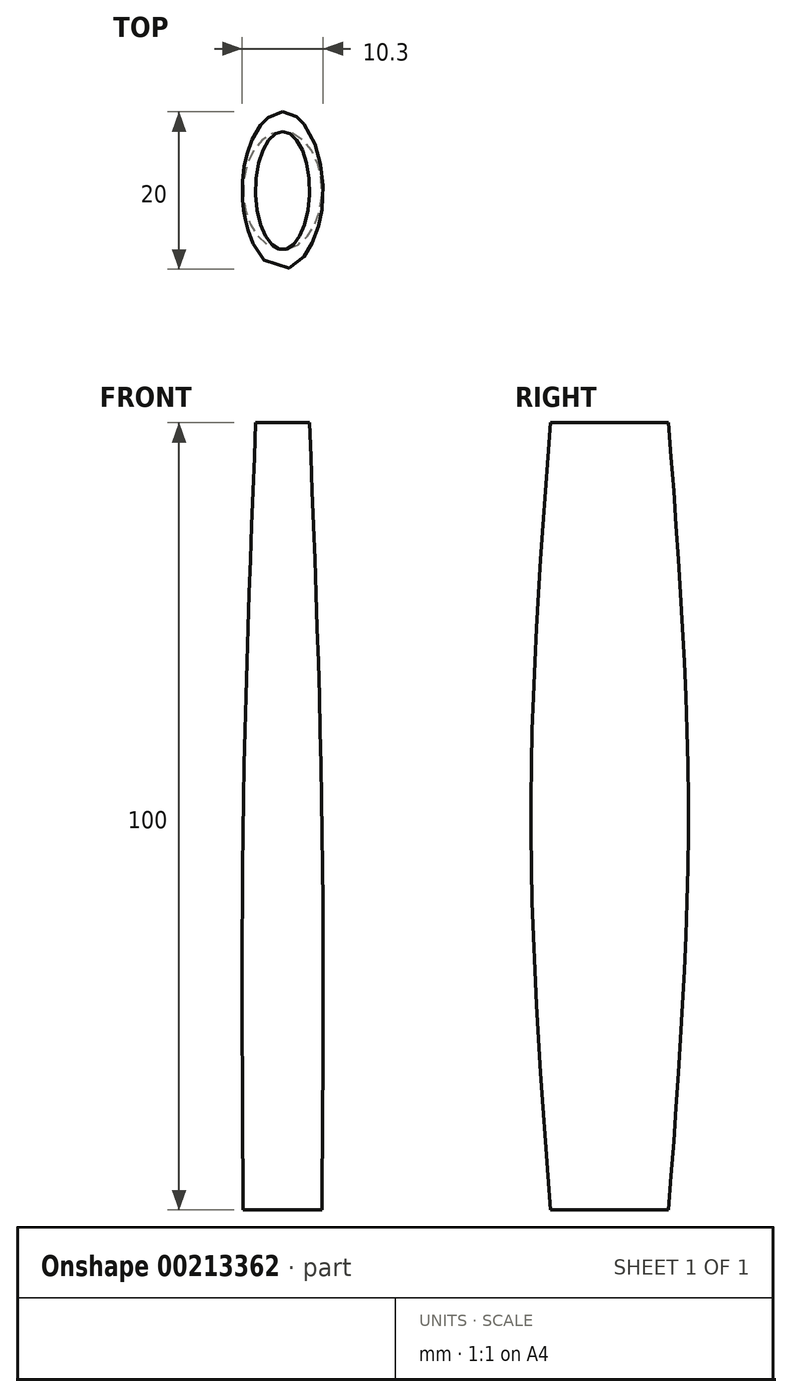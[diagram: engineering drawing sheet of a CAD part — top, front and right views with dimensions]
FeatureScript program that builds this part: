
annotation { "Feature Type Name" : "Feature", "Feature Type Description" : "" }
export const myFeature = defineFeature(function(context is Context, id is Id, definition is map)
    precondition{}
    {
        {
            var Q0;
            Q0=qCreatedBy(makeId("Top.planeOp"),FACE);
            cPlane(context, id + "F0", {"entities" : qUnion([Q0]), "cplaneType" : CPlaneType.OFFSET, "offset" : 50 * mm, "width" : 150 * mm, "height" : 150 * mm});
        }
        {
            var Q0;
            Q0=qCreatedBy(makeId("Top.planeOp"),FACE);
            cPlane(context, id + "F1", {"entities" : qUnion([Q0]), "cplaneType" : CPlaneType.OFFSET, "offset" : 50 * mm, "oppositeDirection" : true, "width" : 150 * mm, "height" : 150 * mm});
        }
        {
            var Q0;
            Q0=qCreatedBy(makeId("Top.planeOp"),FACE);
            var sketch = newSketch(context, id + "F2", { "sketchPlane" : qUnion([Q0])});
            skEllipse(sketch, "E0", {"center": v(0, 0) * mm, "majorRadius": 10 * mm, "minorRadius": 5 * mm, "majorAxis": v(0, 1)});
            skSolve(sketch);
        }
        {
            var Q0;
            Q0=qCreatedBy(id+"F0.planeOp",FACE);
            var sketch = newSketch(context, id + "F3", { "sketchPlane" : qUnion([Q0])});
            skEllipse(sketch, "E1", {"center": v(0, 0) * mm, "majorRadius": 7.5 * mm, "minorRadius": 3.42 * mm, "majorAxis": v(0, 1)});
            skSolve(sketch);
        }
        {
            var Q0;
            Q0=qCreatedBy(id+"F1.planeOp",FACE);
            var sketch = newSketch(context, id + "F4", { "sketchPlane" : qUnion([Q0])});
            skEllipse(sketch, "E2", {"center": v(0, 0) * mm, "majorRadius": 7.5 * mm, "minorRadius": 5 * mm, "majorAxis": v(0, -1)});
            skSolve(sketch);
        }
        {
            var Q0;
            Q0=makeQuery(id+"F3.imprint","IMPRINT",FACE,{"disambiguationData":[TD([[makeQuery(id+"F3.imprint","IMPRINT",EDGE,{"derivedFrom":sQuery(id+"F3.wireOp",EDGE,"E1")}),1.0]])]});
            var Q1;
            Q1=makeQuery(id+"F2.imprint","IMPRINT",FACE,{"disambiguationData":[TD([[makeQuery(id+"F2.imprint","IMPRINT",EDGE,{"derivedFrom":sQuery(id+"F2.wireOp",EDGE,"E0")}),1.0]])]});
            var Q2;
            Q2=makeQuery(id+"F4.imprint","IMPRINT",FACE,{"disambiguationData":[TD([[makeQuery(id+"F4.imprint","IMPRINT",EDGE,{"derivedFrom":sQuery(id+"F4.wireOp",EDGE,"E2")}),1.0]])]});
            loft(context, id + "F5", {"sheetProfilesArray" : [{ "sheetProfileEntities" : qUnion([Q0]) }, { "sheetProfileEntities" : qUnion([Q1]) }, { "sheetProfileEntities" : qUnion([Q2]) }]});
        }
    });
